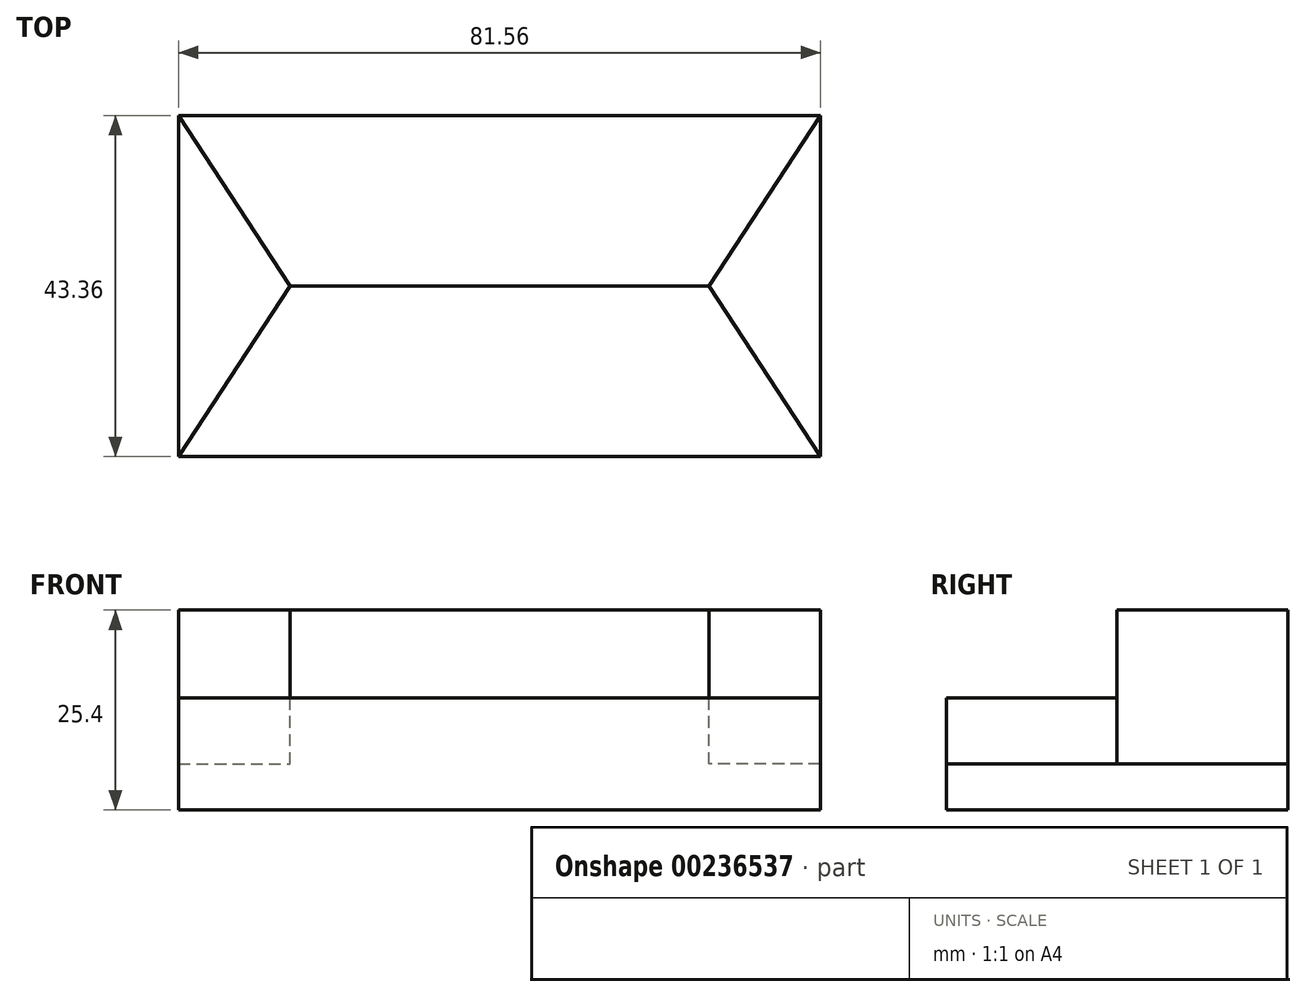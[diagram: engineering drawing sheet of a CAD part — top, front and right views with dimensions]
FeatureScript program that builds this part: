
annotation { "Feature Type Name" : "Feature", "Feature Type Description" : "" }
export const myFeature = defineFeature(function(context is Context, id is Id, definition is map)
    precondition{}
    {
        {
            var Q0;
            Q0=qCreatedBy(makeId("Top.planeOp"),FACE);
            var sketch = newSketch(context, id + "F0", { "sketchPlane" : qUnion([Q0])});
            skLineSegment(sketch, "E0.bottom", {"start": v(-38.46, 17.55) * mm, "end": v(43.1, 17.55) * mm});
            skLineSegment(sketch, "E0.top", {"start": v(-38.46, -25.8) * mm, "end": v(43.1, -25.8) * mm});
            skLineSegment(sketch, "E0.left", {"start": v(-38.46, 17.55) * mm, "end": v(-38.46, -25.8) * mm});
            skLineSegment(sketch, "E0.right", {"start": v(43.1, 17.55) * mm, "end": v(43.1, -25.8) * mm});
            skSolve(sketch);
        }
        {
            var Q0;
            Q0=makeQuery(id+"F0.imprint","IMPRINT",FACE,{"disambiguationData":[TD([[makeQuery(id+"F0.imprint","IMPRINT",EDGE,{"derivedFrom":sQuery(id+"F0.wireOp",EDGE,"E0.bottom")}),-1.0]])]});
            extrude(context, id + "F1", {"entities" : qUnion([Q0]), "depth" : 25.4 * mm});
        }
        {
            var Q0;
            Q0=makeQuery(id+"F1.opExtrude","CAP_FACE",FACE,{"disambiguationData":[OSD([sQuery(id+"F0.wireOp",EDGE,"E0.bottom"),sQuery(id+"F0.wireOp",EDGE,"E0.top"),sQuery(id+"F0.wireOp",EDGE,"E0.left"),sQuery(id+"F0.wireOp",EDGE,"E0.right")])],"isStart":false});
            var sketch = newSketch(context, id + "F2", { "sketchPlane" : qUnion([Q0])});
            skLineSegment(sketch, "E1", {"start": v(-38.46, 17.55) * mm, "end": v(-24.26, -4.13) * mm});
            skPoint(sketch, "E1.endSnap0", {"position": v(-38.46, -4.13) * mm});
            skLineSegment(sketch, "E2", {"start": v(-38.46, -25.8) * mm, "end": v(-24.26, -4.13) * mm});
            skLineSegment(sketch, "E3", {"start": v(-38.46, 17.55) * mm, "end": v(-38.46, -25.8) * mm});
            skLineSegment(sketch, "E4", {"start": v(43.1, 17.55) * mm, "end": v(28.9, -4.13) * mm});
            skLineSegment(sketch, "E5", {"start": v(28.9, -4.13) * mm, "end": v(43.1, -25.8) * mm});
            skLineSegment(sketch, "E6", {"start": v(43.1, 17.55) * mm, "end": v(43.1, -25.8) * mm});
            skSolve(sketch);
        }
        {
            var Q0;
            Q0=makeQuery(id+"F2.imprint","IMPRINT",FACE,{"disambiguationData":[TD([[makeQuery(id+"F2.imprint","IMPRINT",EDGE,{"derivedFrom":sQuery(id+"F2.wireOp",EDGE,"E1")}),-1.0]])]});
            var Q1;
            Q1=makeQuery(id+"F2.imprint","IMPRINT",FACE,{"disambiguationData":[TD([[makeQuery(id+"F2.imprint","IMPRINT",EDGE,{"derivedFrom":sQuery(id+"F2.wireOp",EDGE,"E4")}),1.0]])]});
            extrude(context, id + "F3", {"entities" : qUnion([Q0, Q1]), "operationType" : NewBodyOperationType.REMOVE, "oppositeDirection" : true, "depth" : 19.56 * mm});
        }
        {
            var Q0;
            Q0=makeQuery(id+"F1.opExtrude","CAP_FACE",FACE,{"disambiguationData":[OSD([sQuery(id+"F0.wireOp",EDGE,"E0.bottom"),sQuery(id+"F0.wireOp",EDGE,"E0.top"),sQuery(id+"F0.wireOp",EDGE,"E0.left"),sQuery(id+"F0.wireOp",EDGE,"E0.right")])],"isStart":false});
            var sketch = newSketch(context, id + "F4", { "sketchPlane" : qUnion([Q0])});
            skLineSegment(sketch, "E7", {"start": v(-38.46, -25.8) * mm, "end": v(-24.26, -4.13) * mm});
            skLineSegment(sketch, "E8", {"start": v(-24.26, -4.13) * mm, "end": v(28.9, -4.13) * mm});
            skLineSegment(sketch, "E9", {"start": v(28.9, -4.13) * mm, "end": v(43.1, -25.8) * mm});
            skLineSegment(sketch, "E10", {"start": v(43.1, -25.8) * mm, "end": v(-38.46, -25.8) * mm});
            skSolve(sketch);
        }
        {
            var Q0;
            Q0=makeQuery(id+"F4.imprint","IMPRINT",FACE,{"disambiguationData":[TD([[makeQuery(id+"F4.imprint","IMPRINT",EDGE,{"derivedFrom":sQuery(id+"F4.wireOp",EDGE,"E7")}),-1.0]])]});
            extrude(context, id + "F5", {"entities" : qUnion([Q0]), "operationType" : NewBodyOperationType.REMOVE, "oppositeDirection" : true, "depth" : 11.18 * mm});
        }
    });
